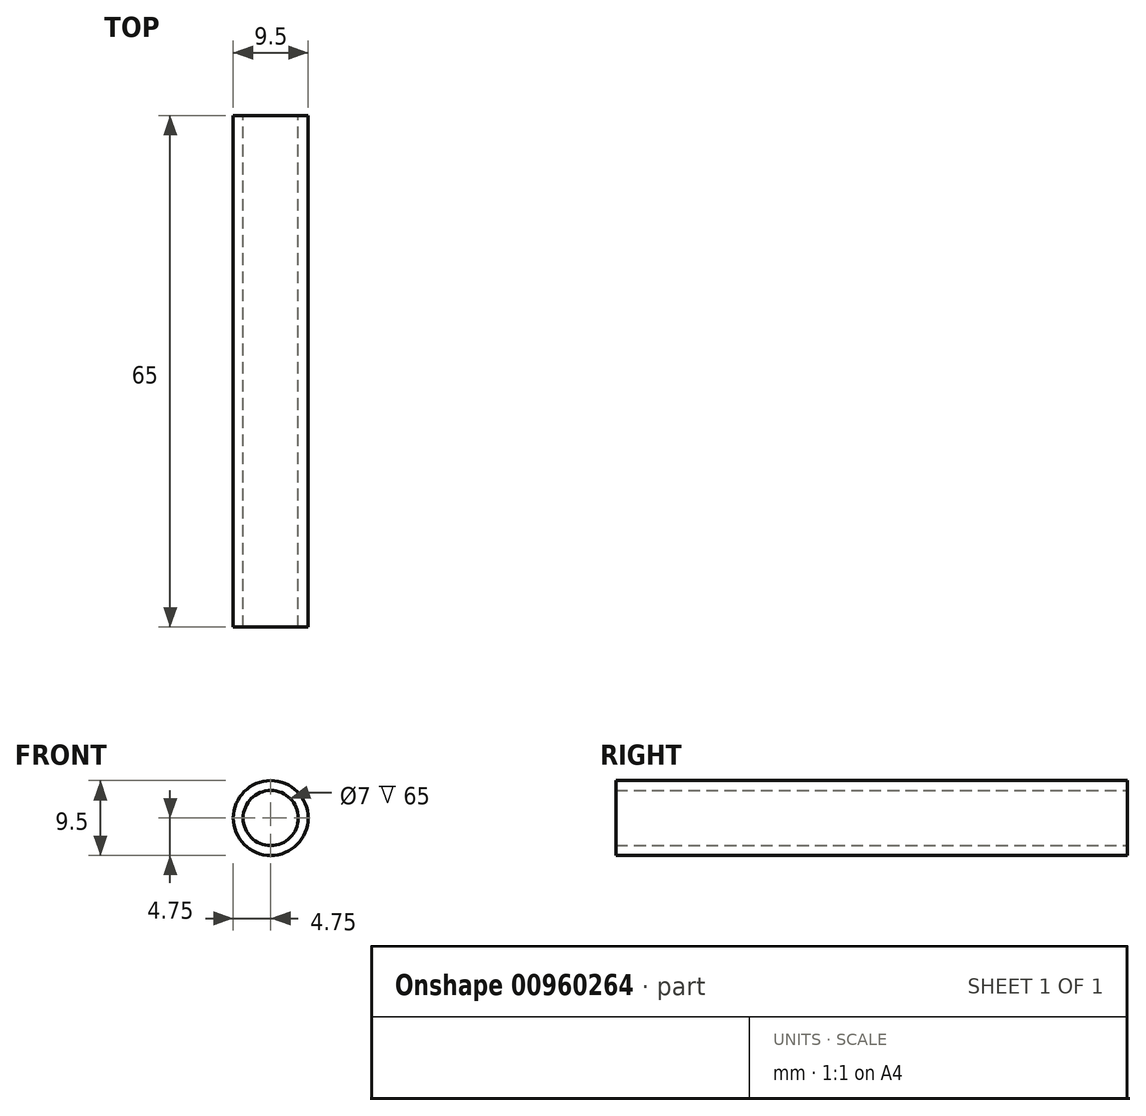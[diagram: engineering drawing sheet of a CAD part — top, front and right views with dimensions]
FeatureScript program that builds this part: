
annotation { "Feature Type Name" : "Feature", "Feature Type Description" : "" }
export const myFeature = defineFeature(function(context is Context, id is Id, definition is map)
    precondition{}
    {
        {
            var Q0;
            Q0=qCreatedBy(makeId("Front.planeOp"),FACE);
            var sketch = newSketch(context, id + "F0", { "sketchPlane" : qUnion([Q0])});
            skCircle(sketch, "E0", {"center": v(0, 0) * mm, "radius": 4.75 * mm});
            skCircle(sketch, "E1", {"center": v(0, 0) * mm, "radius": 3.5 * mm});
            skSolve(sketch);
        }
        {
            var Q0;
            Q0 = qSketchRegion(id + "F0", true);
            extrude(context, id + "F1", {"entities" : qUnion([Q0]), "depth" : 65 * mm, "offsetDistance" : 25 * mm});
        }
    });
